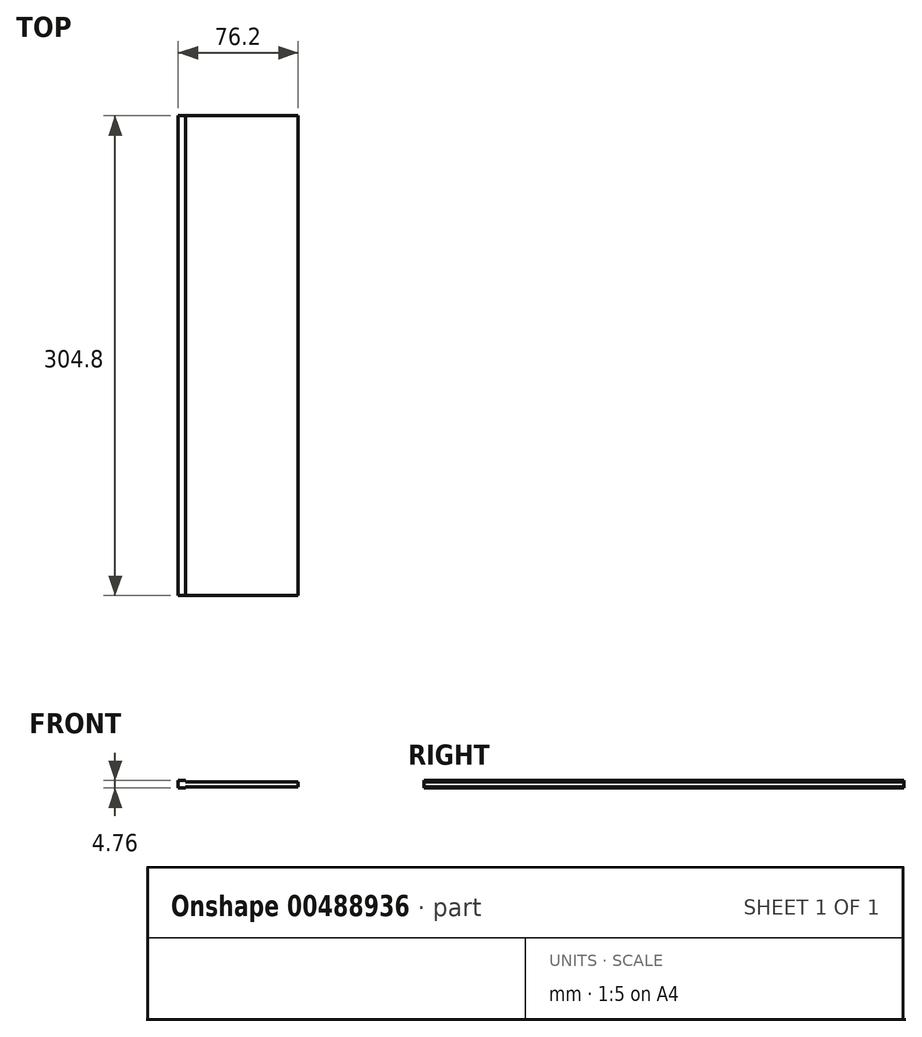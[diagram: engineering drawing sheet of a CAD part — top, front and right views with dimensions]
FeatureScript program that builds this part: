
annotation { "Feature Type Name" : "Feature", "Feature Type Description" : "" }
export const myFeature = defineFeature(function(context is Context, id is Id, definition is map)
    precondition{}
    {
        {
            var Q0;
            Q0=qCreatedBy(makeId("Front.planeOp"),FACE);
            var sketch = newSketch(context, id + "F0", { "sketchPlane" : qUnion([Q0])});
            skLineSegment(sketch, "E0.bottom", {"start": v(0, 0) * mm, "end": v(4.76, 0) * mm});
            skLineSegment(sketch, "E0.top", {"start": v(0, 4.76) * mm, "end": v(4.76, 4.76) * mm});
            skLineSegment(sketch, "E0.left", {"start": v(0, 0) * mm, "end": v(0, 4.76) * mm});
            skLineSegment(sketch, "E0.right", {"start": v(4.76, 0) * mm, "end": v(4.76, 4.76) * mm});
            skLineSegment(sketch, "E1.bottom", {"start": v(4.76, 3.97) * mm, "end": v(76.2, 3.97) * mm});
            skLineSegment(sketch, "E1.top", {"start": v(4.76, 0.8) * mm, "end": v(76.2, 0.8) * mm});
            skLineSegment(sketch, "E1.left", {"start": v(4.76, 3.97) * mm, "end": v(4.76, 0.8) * mm});
            skLineSegment(sketch, "E1.right", {"start": v(76.2, 3.97) * mm, "end": v(76.2, 0.8) * mm});
            skPoint(sketch, "E2", {"position": v(4.76, 2.38) * mm});
            skSolve(sketch);
        }
        {
            var Q0;
            Q0 = qSketchRegion(id + "F0", true);
            extrude(context, id + "F1", {"entities" : qUnion([Q0]), "depth" : 304.8 * mm});
        }
    });
